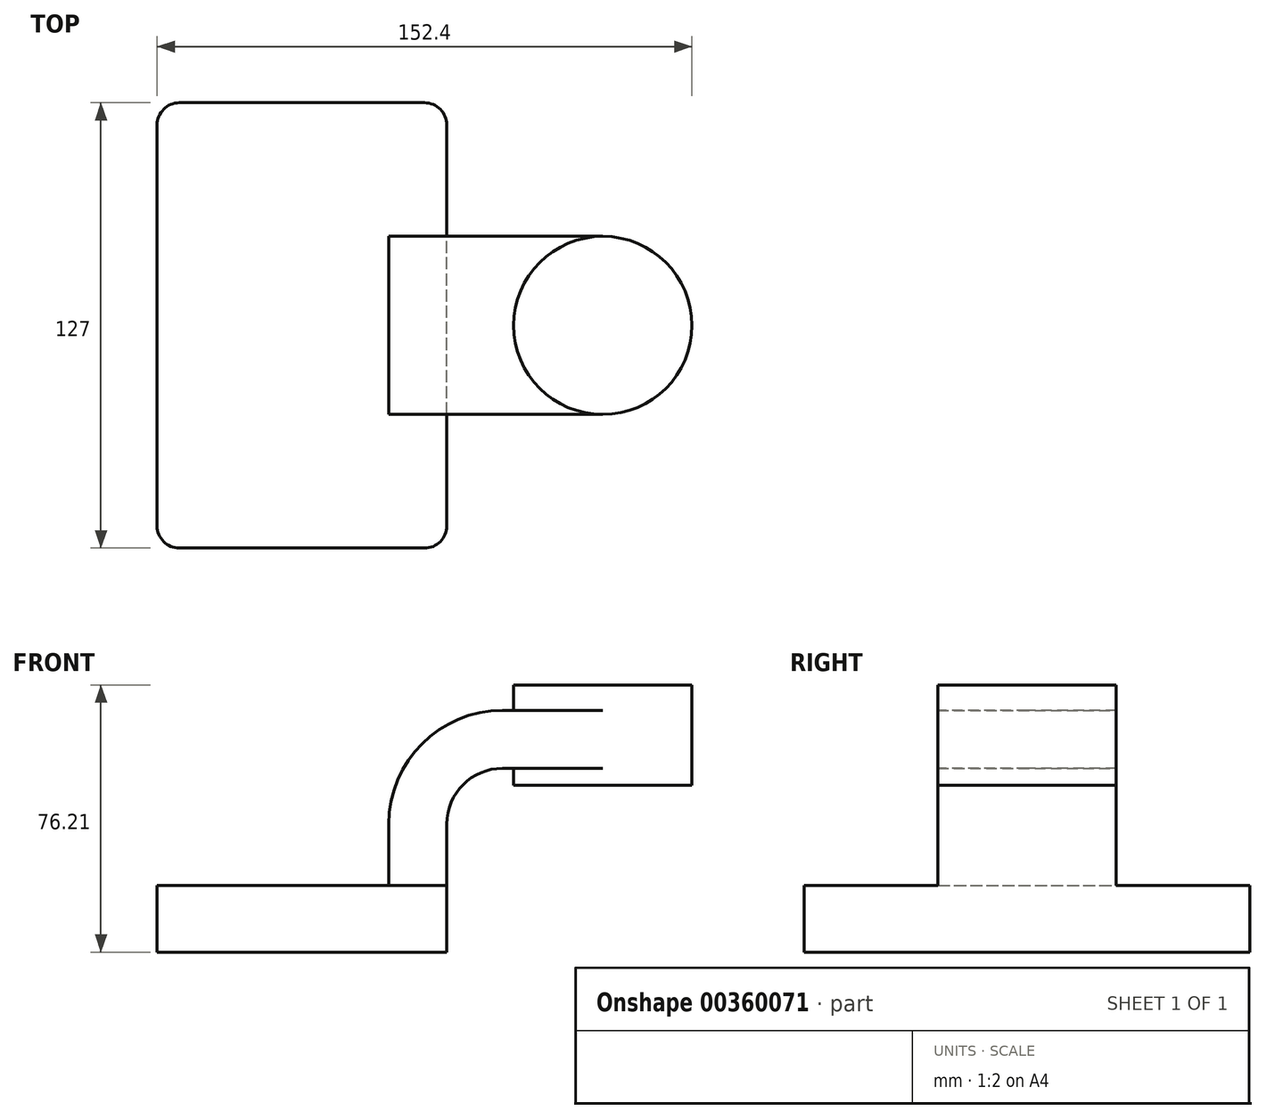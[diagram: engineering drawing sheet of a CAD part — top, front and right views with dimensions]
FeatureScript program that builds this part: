
annotation { "Feature Type Name" : "Feature", "Feature Type Description" : "" }
export const myFeature = defineFeature(function(context is Context, id is Id, definition is map)
    precondition{}
    {
        {
            var Q0;
            Q0=qCreatedBy(makeId("Front.planeOp"),FACE);
            var sketch = newSketch(context, id + "F0", { "sketchPlane" : qUnion([Q0])});
            skLineSegment(sketch, "E0.bottom", {"start": v(-41.28, 9.52) * mm, "end": v(41.27, 9.53) * mm});
            skLineSegment(sketch, "E0.top", {"start": v(-41.28, -9.52) * mm, "end": v(41.28, -9.52) * mm});
            skLineSegment(sketch, "E0.left", {"start": v(-41.28, 9.52) * mm, "end": v(-41.28, -9.53) * mm});
            skLineSegment(sketch, "E0.right", {"start": v(41.27, 9.53) * mm, "end": v(41.28, -9.52) * mm});
            skPoint(sketch, "E0.middle", {"position": v(0, 0) * mm});
            skLineSegment(sketch, "E1.bottom", {"start": v(60.32, 38.1) * mm, "end": v(111.12, 38.1) * mm});
            skLineSegment(sketch, "E1.top", {"start": v(60.32, 66.68) * mm, "end": v(111.12, 66.68) * mm});
            skLineSegment(sketch, "E1.left", {"start": v(60.32, 38.1) * mm, "end": v(60.32, 66.68) * mm});
            skLineSegment(sketch, "E1.right", {"start": v(111.12, 38.1) * mm, "end": v(111.12, 66.68) * mm});
            skPoint(sketch, "E1.middle", {"position": v(85.72, 52.39) * mm});
            skLineSegment(sketch, "E2", {"start": v(41.27, 9.53) * mm, "end": v(41.27, 27) * mm});
            skArc(sketch, "E3", {"start": v(41.27, 27) * mm, "mid": v(45.92, 38.23) * mm, "end": v(57.15, 42.88) * mm});
            skLineSegment(sketch, "E4", {"start": v(57.15, 42.88) * mm, "end": v(85.72, 42.88) * mm});
            skLineSegment(sketch, "E5.0", {"start": v(57.15, 59.4) * mm, "end": v(85.72, 59.4) * mm});
            skArc(sketch, "E5.1", {"start": v(24.74, 27) * mm, "mid": v(34.24, 49.91) * mm, "end": v(57.15, 59.4) * mm});
            skLineSegment(sketch, "E5.2", {"start": v(24.74, 9.53) * mm, "end": v(24.74, 27) * mm});
            skFitSpline(sketch, "E6", {"points": [v(-41.28, 9.53) * mm, v(57.15, 59.4) * mm], "startDerivative": vector(-1.33, 103.37) * mm, "endDerivative": vector(118.21, -3.17) * mm});
            skLineSegment(sketch, "E7", {"start": v(85.72, 38.1) * mm, "end": v(85.72, 66.68) * mm});
            skSolve(sketch);
        }
        {
            var Q0;
            Q0=makeQuery(id+"F0.imprint","IMPRINT",FACE,{"disambiguationData":[TD([[makeQuery(id+"F0.imprint","IMPRINT",EDGE,{"derivedFrom":sQuery(id+"F0.wireOp",EDGE,"E0.top")}),1.0]])]});
            extrude(context, id + "F1", {"entities" : qUnion([Q0]), "endBound" : BoundingType.SYMMETRIC, "depth" : 127 * mm});
        }
        {
            var Q0;
            {var subQ1=sQuery(id+"F0.wireOp",EDGE,"E2");Q0=makeQuery(id+"F0.imprint","IMPRINT",FACE,{"disambiguationData":[TD([[makeQuery(id+"F0.imprint","IMPRINT",EDGE,{"derivedFrom":subQ1}),1.0]])]});}
            var Q1;
            {var subQ0=sQuery(id+"F0.wireOp",EDGE,"E4");var subQ1=sQuery(id+"F0.wireOp",EDGE,"E1.left");var subQ2=makeQuery(id+"F0.imprint","INTERSECT",VERTEX,{"derivedFrom":[subQ1,subQ0]});Q1=makeQuery(id+"F0.imprint","IMPRINT",FACE,{"disambiguationData":[TD([[makeQuery(id+"F0.imprint","IMPRINT",EDGE,{"disambiguationData":[TD([[subQ2,-1.0]])],"derivedFrom":subQ1}),-1.0]])]});}
            extrude(context, id + "F2", {"entities" : qUnion([Q0, Q1]), "operationType" : NewBodyOperationType.ADD, "endBound" : BoundingType.SYMMETRIC, "depth" : 50.8 * mm});
        }
        {
            var Q0;
            Q0=makeQuery(id+"F0.imprint","IMPRINT",FACE,{"disambiguationData":[TD([[makeQuery(id+"F0.imprint","IMPRINT",EDGE,{"derivedFrom":sQuery(id+"F0.wireOp",EDGE,"E5.1")}),1.0]])]});
            extrude(context, id + "F3", {"entities" : qUnion([Q0]), "operationType" : NewBodyOperationType.ADD, "endBound" : BoundingType.SYMMETRIC, "depth" : 15.88 * mm});
        }
        {
            var Q0;
            {var subQ4=sQuery(id+"F0.wireOp",EDGE,"E1.right");Q0=makeQuery(id+"F0.imprint","IMPRINT",FACE,{"disambiguationData":[TD([[makeQuery(id+"F0.imprint","IMPRINT",EDGE,{"derivedFrom":subQ4}),1.0]])]});}
            var Q1;
            Q1=sQuery(id+"F0.wireOp",EDGE,"E7");
            revolve(context, id + "F4", {"operationType" : NewBodyOperationType.ADD, "entities" : qUnion([Q0]), "axis" : qUnion([Q1]), "revolveType" : RevolveType.FULL});
        }
        {
            var Q0;
            Q0=makeQuery(id+"F1.opExtrude","CAP_EDGE",EDGE,{"disambiguationData":[OSD([sQuery(id+"F0.wireOp",EDGE,"E0.left")])],"isStart":false});
            var Q1;
            Q1=makeQuery(id+"F1.opExtrude","CAP_EDGE",EDGE,{"disambiguationData":[OSD([sQuery(id+"F0.wireOp",EDGE,"E0.right")])],"isStart":false});
            var Q2;
            Q2=makeQuery(id+"F1.opExtrude","CAP_EDGE",EDGE,{"disambiguationData":[OSD([sQuery(id+"F0.wireOp",EDGE,"E0.right")])],"isStart":true});
            var Q3;
            Q3=makeQuery(id+"F1.opExtrude","CAP_EDGE",EDGE,{"disambiguationData":[OSD([sQuery(id+"F0.wireOp",EDGE,"E0.left")])],"isStart":true});
            fillet(context, id + "F5", {"entities" : qUnion([Q0, Q1, Q2, Q3]), "radius" : 6.35 * mm, "tangentPropagation" : true, "allowEdgeOverflow" : false});
        }
    });
